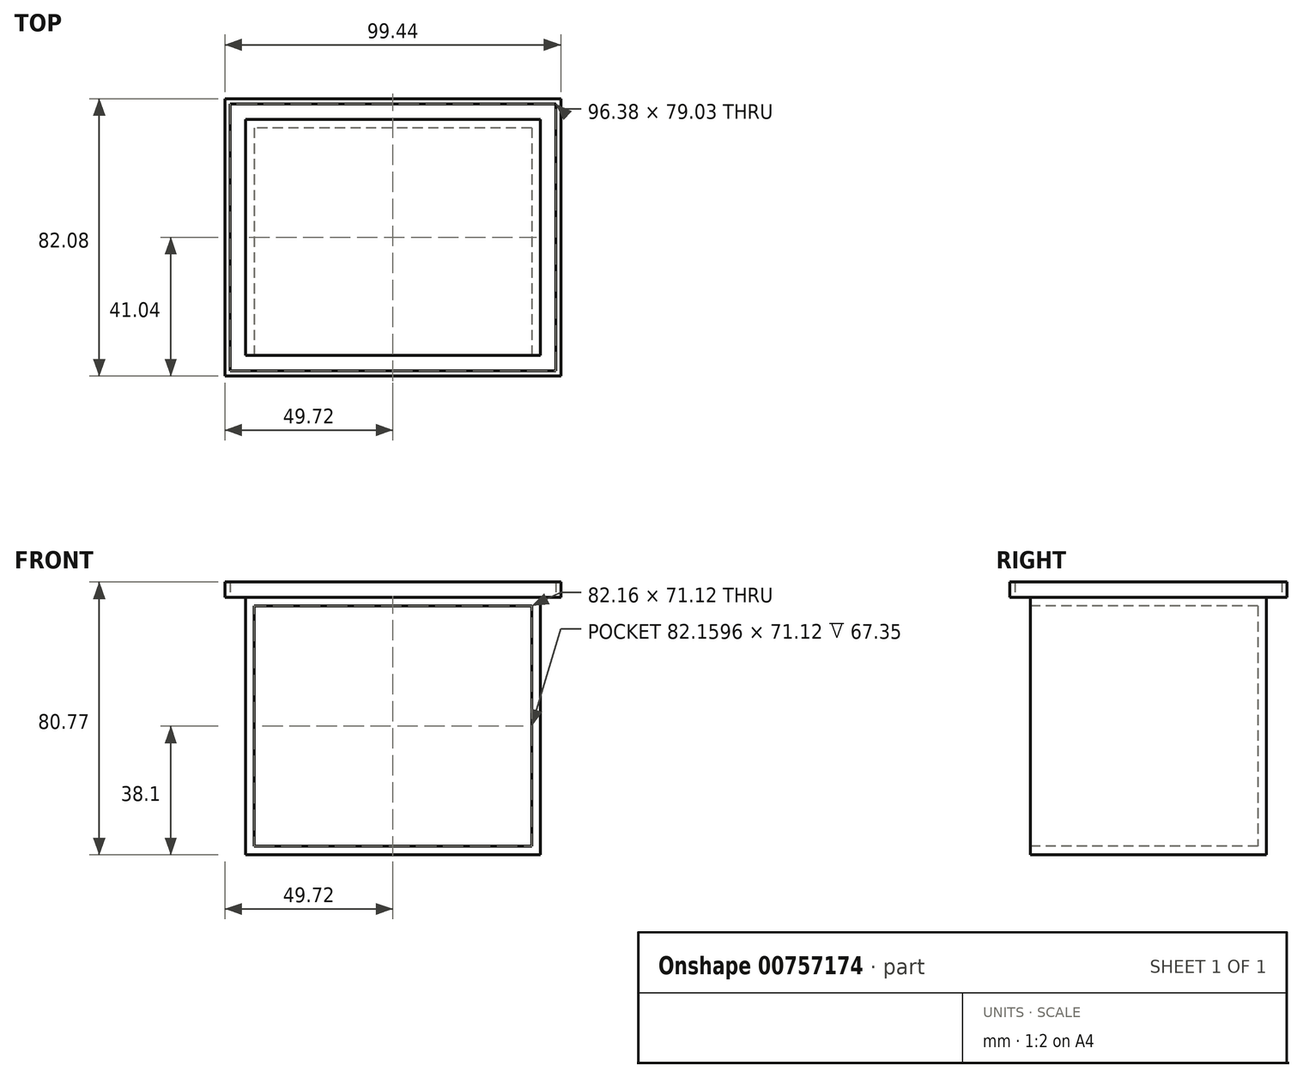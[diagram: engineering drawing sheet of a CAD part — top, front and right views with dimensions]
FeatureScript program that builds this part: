
annotation { "Feature Type Name" : "Feature", "Feature Type Description" : "" }
export const myFeature = defineFeature(function(context is Context, id is Id, definition is map)
    precondition{}
    {
        {
            var Q0;
            Q0=qCreatedBy(makeId("Top.planeOp"),FACE);
            var sketch = newSketch(context, id + "F0", { "sketchPlane" : qUnion([Q0])});
            skLineSegment(sketch, "E0.bottom", {"start": v(43.62, 34.95) * mm, "end": v(-43.62, 34.95) * mm});
            skLineSegment(sketch, "E0.top", {"start": v(43.62, -34.95) * mm, "end": v(-43.62, -34.95) * mm});
            skLineSegment(sketch, "E0.left", {"start": v(43.62, 34.95) * mm, "end": v(43.62, -34.95) * mm});
            skLineSegment(sketch, "E0.right", {"start": v(-43.62, 34.95) * mm, "end": v(-43.62, -34.95) * mm});
            skPoint(sketch, "E0.middle", {"position": v(0, 0) * mm});
            skSolve(sketch);
        }
        {
            var Q0;
            Q0 = qSketchRegion(id + "F0", true);
            extrude(context, id + "F1", {"entities" : qUnion([Q0]), "depth" : 76.2 * mm, "offsetDistance" : 25.4 * mm});
        }
        {
            var Q0;
            Q0=makeQuery(id+"F1.opExtrude","SWEPT_FACE",FACE,{"disambiguationData":[OSD([sQuery(id+"F0.wireOp",EDGE,"E0.top")])]});
            shell(context, id + "F2", {"entities" : qUnion([Q0]), "thickness" : 2.54 * mm});
        }
        {
            var Q0;
            Q0=makeQuery(id+"F1.opExtrude","CAP_FACE",FACE,{"disambiguationData":[OSD([sQuery(id+"F0.wireOp",EDGE,"E0.bottom"),sQuery(id+"F0.wireOp",EDGE,"E0.top"),sQuery(id+"F0.wireOp",EDGE,"E0.left"),sQuery(id+"F0.wireOp",EDGE,"E0.right")])],"isStart":false});
            var sketch = newSketch(context, id + "F3", { "sketchPlane" : qUnion([Q0])});
            skLineSegment(sketch, "E1.0", {"start": v(-49.72, -41.04) * mm, "end": v(49.72, -41.04) * mm});
            skLineSegment(sketch, "E1.1", {"start": v(-49.72, 41.04) * mm, "end": v(-49.72, -41.04) * mm});
            skLineSegment(sketch, "E1.2", {"start": v(49.72, 41.04) * mm, "end": v(-49.72, 41.04) * mm});
            skLineSegment(sketch, "E1.3", {"start": v(49.72, -41.04) * mm, "end": v(49.72, 41.04) * mm});
            skLineSegment(sketch, "E2.0", {"start": v(-48.2, -39.52) * mm, "end": v(48.2, -39.52) * mm});
            skLineSegment(sketch, "E2.1", {"start": v(-48.2, 39.52) * mm, "end": v(-48.2, -39.52) * mm});
            skLineSegment(sketch, "E2.2", {"start": v(48.2, 39.52) * mm, "end": v(-48.2, 39.52) * mm});
            skLineSegment(sketch, "E2.3", {"start": v(48.2, -39.52) * mm, "end": v(48.2, 39.52) * mm});
            skSolve(sketch);
        }
        {
            var Q0;
            Q0 = qSketchRegion(id + "F3", true);
            extrude(context, id + "F4", {"entities" : qUnion([Q0]), "operationType" : NewBodyOperationType.ADD, "depth" : 4.57 * mm, "offsetDistance" : 25.4 * mm});
        }
    });
